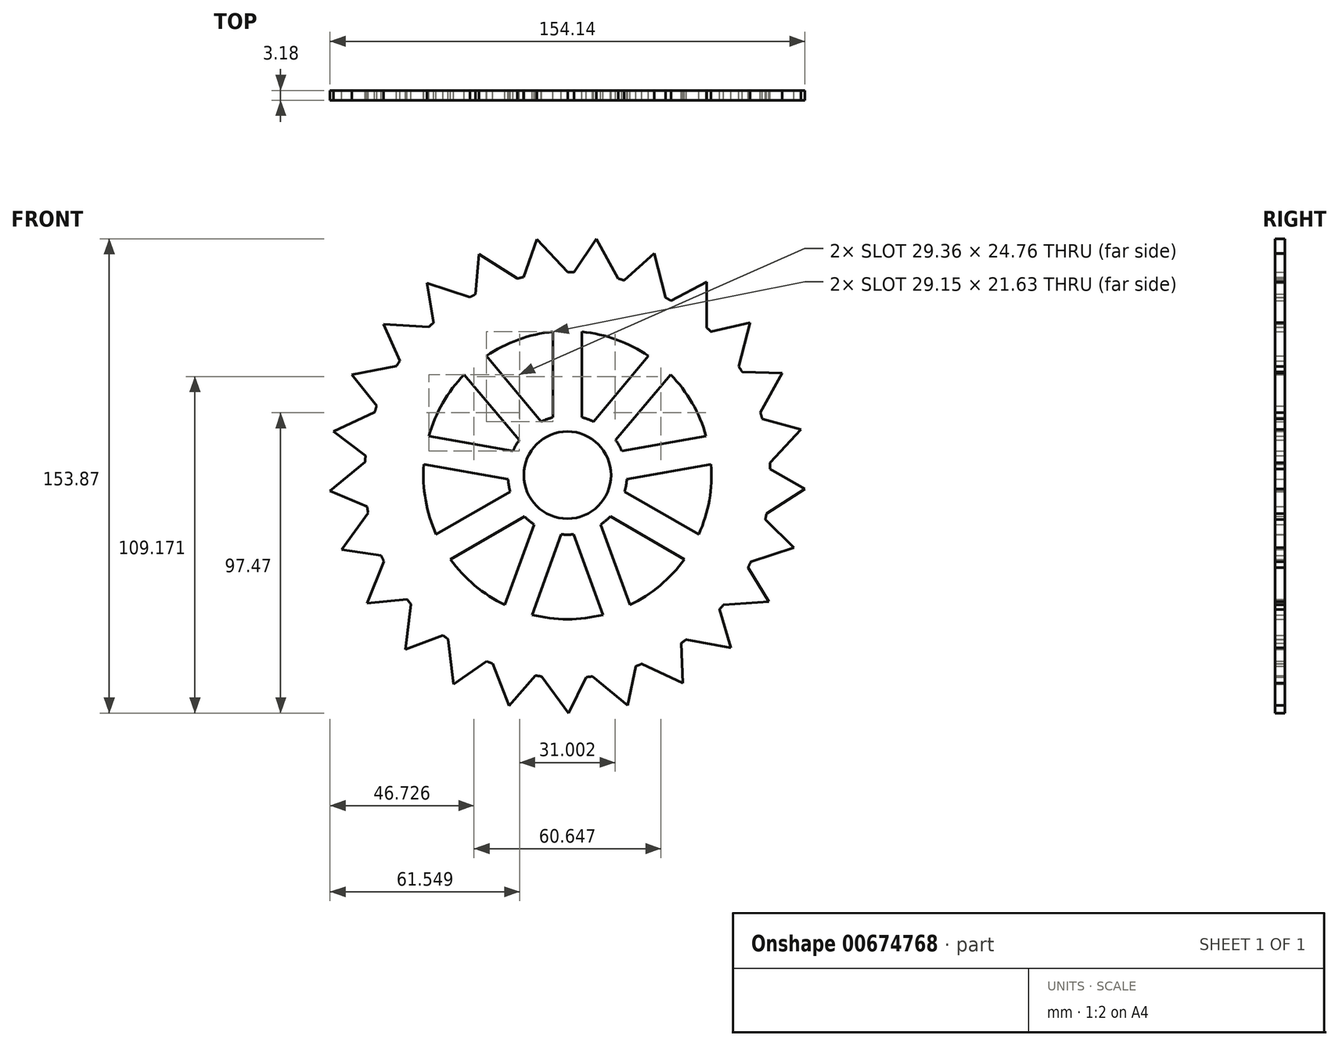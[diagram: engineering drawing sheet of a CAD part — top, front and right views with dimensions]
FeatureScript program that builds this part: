
annotation { "Feature Type Name" : "Feature", "Feature Type Description" : "" }
export const myFeature = defineFeature(function(context is Context, id is Id, definition is map)
    precondition{}
    {
        {
            var Q0;
            Q0=qCreatedBy(makeId("Front.planeOp"),FACE);
            var sketch = newSketch(context, id + "F0", { "sketchPlane" : qUnion([Q0])});
            skCircle(sketch, "E0", {"center": v(0, 0) * mm, "radius": 65.84 * mm});
            skLineSegment(sketch, "E1", {"start": v(33.58, 56.64) * mm, "end": v(45.14, 62.65) * mm});
            skLineSegment(sketch, "E2", {"start": v(45.14, 62.65) * mm, "end": v(45.14, 47.93) * mm});
            skLineSegment(sketch, "E3.1.0", {"start": v(28.14, 71.91) * mm, "end": v(31.8, 57.65) * mm});
            skLineSegment(sketch, "E3.1.1", {"start": v(18.44, 63.21) * mm, "end": v(28.14, 71.91) * mm});
            skLineSegment(sketch, "E3.2.0", {"start": v(9.38, 76.65) * mm, "end": v(16.47, 63.75) * mm});
            skLineSegment(sketch, "E3.2.1", {"start": v(2.14, 65.8) * mm, "end": v(9.38, 76.65) * mm});
            skLineSegment(sketch, "E3.3.0", {"start": v(-9.98, 76.57) * mm, "end": v(0.1, 65.84) * mm});
            skLineSegment(sketch, "E3.3.1", {"start": v(-14.3, 64.27) * mm, "end": v(-9.98, 76.57) * mm});
            skLineSegment(sketch, "E3.4.0", {"start": v(-28.7, 71.69) * mm, "end": v(-16.28, 63.8) * mm});
            skLineSegment(sketch, "E3.4.1", {"start": v(-29.83, 58.7) * mm, "end": v(-28.7, 71.69) * mm});
            skLineSegment(sketch, "E3.5.0", {"start": v(-45.63, 62.3) * mm, "end": v(-31.64, 57.75) * mm});
            skLineSegment(sketch, "E3.5.1", {"start": v(-43.49, 49.44) * mm, "end": v(-45.63, 62.3) * mm});
            skLineSegment(sketch, "E3.6.0", {"start": v(-59.7, 48.99) * mm, "end": v(-45, 48.06) * mm});
            skLineSegment(sketch, "E3.6.1", {"start": v(-54.42, 37.07) * mm, "end": v(-59.7, 48.99) * mm});
            skLineSegment(sketch, "E3.7.0", {"start": v(-70, 32.6) * mm, "end": v(-55.54, 35.36) * mm});
            skLineSegment(sketch, "E3.7.1", {"start": v(-61.93, 22.37) * mm, "end": v(-70, 32.6) * mm});
            skLineSegment(sketch, "E3.8.0", {"start": v(-75.91, 14.17) * mm, "end": v(-62.6, 20.44) * mm});
            skLineSegment(sketch, "E3.8.1", {"start": v(-65.55, 6.27) * mm, "end": v(-75.91, 14.17) * mm});
            skLineSegment(sketch, "E3.9.0", {"start": v(-77.05, -5.15) * mm, "end": v(-65.7, 4.23) * mm});
            skLineSegment(sketch, "E3.9.1", {"start": v(-65.05, -10.23) * mm, "end": v(-77.05, -5.15) * mm});
            skLineSegment(sketch, "E3.10.0", {"start": v(-73.35, -24.15) * mm, "end": v(-64.7, -12.24) * mm});
            skLineSegment(sketch, "E3.10.1", {"start": v(-60.46, -26.08) * mm, "end": v(-73.35, -24.15) * mm});
            skLineSegment(sketch, "E3.11.0", {"start": v(-65.04, -41.63) * mm, "end": v(-59.62, -27.95) * mm});
            skLineSegment(sketch, "E3.11.1", {"start": v(-52.07, -40.3) * mm, "end": v(-65.04, -41.63) * mm});
            skLineSegment(sketch, "E3.12.0", {"start": v(-52.64, -56.5) * mm, "end": v(-50.8, -41.9) * mm});
            skLineSegment(sketch, "E3.12.1", {"start": v(-40.41, -51.98) * mm, "end": v(-52.64, -56.5) * mm});
            skLineSegment(sketch, "E3.13.0", {"start": v(-36.94, -67.82) * mm, "end": v(-38.78, -53.21) * mm});
            skLineSegment(sketch, "E3.13.1", {"start": v(-26.22, -60.4) * mm, "end": v(-36.94, -67.82) * mm});
            skLineSegment(sketch, "E3.14.0", {"start": v(-18.91, -74.87) * mm, "end": v(-24.33, -61.19) * mm});
            skLineSegment(sketch, "E3.14.1", {"start": v(-10.37, -65.02) * mm, "end": v(-18.91, -74.87) * mm});
            skLineSegment(sketch, "E3.15.0", {"start": v(0.3, -77.22) * mm, "end": v(-8.35, -65.31) * mm});
            skLineSegment(sketch, "E3.15.1", {"start": v(6.12, -65.56) * mm, "end": v(0.3, -77.22) * mm});
            skLineSegment(sketch, "E3.16.0", {"start": v(19.5, -74.72) * mm, "end": v(8.16, -65.34) * mm});
            skLineSegment(sketch, "E3.16.1", {"start": v(22.24, -61.98) * mm, "end": v(19.5, -74.72) * mm});
            skLineSegment(sketch, "E3.17.0", {"start": v(37.47, -67.52) * mm, "end": v(24.15, -61.26) * mm});
            skLineSegment(sketch, "E3.17.1", {"start": v(36.95, -54.5) * mm, "end": v(37.47, -67.52) * mm});
            skLineSegment(sketch, "E3.18.0", {"start": v(53.08, -56.08) * mm, "end": v(38.62, -53.33) * mm});
            skLineSegment(sketch, "E3.18.1", {"start": v(49.34, -43.6) * mm, "end": v(53.08, -56.08) * mm});
            skLineSegment(sketch, "E3.19.0", {"start": v(65.36, -41.12) * mm, "end": v(50.67, -42.05) * mm});
            skLineSegment(sketch, "E3.19.1", {"start": v(58.64, -29.96) * mm, "end": v(65.36, -41.12) * mm});
            skLineSegment(sketch, "E3.20.0", {"start": v(73.54, -23.57) * mm, "end": v(59.54, -28.12) * mm});
            skLineSegment(sketch, "E3.20.1", {"start": v(64.24, -14.43) * mm, "end": v(73.54, -23.57) * mm});
            skLineSegment(sketch, "E3.21.0", {"start": v(77.09, -4.55) * mm, "end": v(64.66, -12.43) * mm});
            skLineSegment(sketch, "E3.21.1", {"start": v(65.81, 2) * mm, "end": v(77.09, -4.55) * mm});
            skLineSegment(sketch, "E3.22.0", {"start": v(75.8, 14.77) * mm, "end": v(65.72, 4.04) * mm});
            skLineSegment(sketch, "E3.22.1", {"start": v(63.25, 18.3) * mm, "end": v(75.8, 14.77) * mm});
            skLineSegment(sketch, "E3.23.0", {"start": v(69.74, 33.15) * mm, "end": v(62.65, 20.26) * mm});
            skLineSegment(sketch, "E3.23.1", {"start": v(56.71, 33.46) * mm, "end": v(69.74, 33.15) * mm});
            skLineSegment(sketch, "E3.24.0", {"start": v(59.3, 49.46) * mm, "end": v(55.65, 35.2) * mm});
            skLineSegment(sketch, "E3.24.1", {"start": v(46.61, 46.5) * mm, "end": v(59.3, 49.46) * mm});
            skCircle(sketch, "E4", {"center": v(0, 0) * mm, "radius": 14.14 * mm});
            skCircle(sketch, "E5", {"center": v(0, 0) * mm, "radius": 46.76 * mm});
            skLineSegment(sketch, "E6", {"start": v(-4.68, 13.35) * mm, "end": v(-4.68, 46.53) * mm});
            skLineSegment(sketch, "E7", {"start": v(4.68, 13.35) * mm, "end": v(4.68, 46.53) * mm});
            skLineSegment(sketch, "E8.1.0", {"start": v(-4.99, 13.23) * mm, "end": v(-26.32, 38.65) * mm});
            skLineSegment(sketch, "E8.1.1", {"start": v(-12.17, 7.21) * mm, "end": v(-33.5, 32.63) * mm});
            skLineSegment(sketch, "E8.2.0", {"start": v(-12.33, 6.93) * mm, "end": v(-45, 12.7) * mm});
            skLineSegment(sketch, "E8.2.1", {"start": v(-13.96, -2.3) * mm, "end": v(-46.63, 3.47) * mm});
            skLineSegment(sketch, "E8.3.0", {"start": v(-13.9, -2.62) * mm, "end": v(-42.63, -19.2) * mm});
            skLineSegment(sketch, "E8.3.1", {"start": v(-9.22, -10.73) * mm, "end": v(-37.95, -27.32) * mm});
            skLineSegment(sketch, "E8.4.0", {"start": v(-8.97, -10.94) * mm, "end": v(-20.31, -42.12) * mm});
            skLineSegment(sketch, "E8.4.1", {"start": v(-0.16, -14.14) * mm, "end": v(-11.51, -45.32) * mm});
            skLineSegment(sketch, "E8.5.0", {"start": v(0.16, -14.14) * mm, "end": v(11.51, -45.32) * mm});
            skLineSegment(sketch, "E8.5.1", {"start": v(8.97, -10.94) * mm, "end": v(20.31, -42.12) * mm});
            skLineSegment(sketch, "E8.6.0", {"start": v(9.22, -10.73) * mm, "end": v(37.95, -27.32) * mm});
            skLineSegment(sketch, "E8.6.1", {"start": v(13.9, -2.62) * mm, "end": v(42.63, -19.2) * mm});
            skLineSegment(sketch, "E8.7.0", {"start": v(13.96, -2.3) * mm, "end": v(46.63, 3.47) * mm});
            skLineSegment(sketch, "E8.7.1", {"start": v(12.33, 6.93) * mm, "end": v(45, 12.7) * mm});
            skLineSegment(sketch, "E8.8.0", {"start": v(12.17, 7.21) * mm, "end": v(33.5, 32.63) * mm});
            skLineSegment(sketch, "E8.8.1", {"start": v(4.99, 13.23) * mm, "end": v(26.32, 38.65) * mm});
            skCircle(sketch, "E9", {"center": v(0, 0) * mm, "radius": 19.33 * mm});
            skSolve(sketch);
        }
        {
            var Q0;
            {var subQ0=sQuery(id+"F0.wireOp",EDGE,"E0");var subQ52=makeQuery(id+"F0.imprint","INTERSECT",VERTEX,{"derivedFrom":[subQ0,sQuery(id+"F0.wireOp",EDGE,"E3.21.1")]});Q0=makeQuery(id+"F0.imprint","IMPRINT",FACE,{"disambiguationData":[TD([[makeQuery(id+"F0.imprint","IMPRINT",EDGE,{"disambiguationData":[TD([[subQ52,-1.0]])],"derivedFrom":subQ0}),1.0]])]});}
            var Q1;
            {var subQ0=sQuery(id+"F0.wireOp",EDGE,"E8.8.0");Q1=makeQuery(id+"F0.imprint","IMPRINT",FACE,{"disambiguationData":[TD([[makeQuery(id+"F0.imprint","IMPRINT",EDGE,{"derivedFrom":subQ0}),1.0]])]});}
            var Q2;
            {var subQ0=sQuery(id+"F0.wireOp",EDGE,"E6");Q2=makeQuery(id+"F0.imprint","IMPRINT",FACE,{"disambiguationData":[TD([[makeQuery(id+"F0.imprint","IMPRINT",EDGE,{"derivedFrom":subQ0}),-1.0]])]});}
            var Q3;
            {var subQ0=sQuery(id+"F0.wireOp",EDGE,"E8.7.0");Q3=makeQuery(id+"F0.imprint","IMPRINT",FACE,{"disambiguationData":[TD([[makeQuery(id+"F0.imprint","IMPRINT",EDGE,{"derivedFrom":subQ0}),1.0]])]});}
            var Q4;
            {var subQ0=sQuery(id+"F0.wireOp",EDGE,"E8.6.0");Q4=makeQuery(id+"F0.imprint","IMPRINT",FACE,{"disambiguationData":[TD([[makeQuery(id+"F0.imprint","IMPRINT",EDGE,{"derivedFrom":subQ0}),1.0]])]});}
            var Q5;
            {var subQ0=sQuery(id+"F0.wireOp",EDGE,"E8.5.0");Q5=makeQuery(id+"F0.imprint","IMPRINT",FACE,{"disambiguationData":[TD([[makeQuery(id+"F0.imprint","IMPRINT",EDGE,{"derivedFrom":subQ0}),1.0]])]});}
            var Q6;
            {var subQ0=sQuery(id+"F0.wireOp",EDGE,"E8.4.0");Q6=makeQuery(id+"F0.imprint","IMPRINT",FACE,{"disambiguationData":[TD([[makeQuery(id+"F0.imprint","IMPRINT",EDGE,{"derivedFrom":subQ0}),1.0]])]});}
            var Q7;
            {var subQ0=sQuery(id+"F0.wireOp",EDGE,"E8.3.0");Q7=makeQuery(id+"F0.imprint","IMPRINT",FACE,{"disambiguationData":[TD([[makeQuery(id+"F0.imprint","IMPRINT",EDGE,{"derivedFrom":subQ0}),1.0]])]});}
            var Q8;
            {var subQ0=sQuery(id+"F0.wireOp",EDGE,"E8.2.0");Q8=makeQuery(id+"F0.imprint","IMPRINT",FACE,{"disambiguationData":[TD([[makeQuery(id+"F0.imprint","IMPRINT",EDGE,{"derivedFrom":subQ0}),1.0]])]});}
            var Q9;
            {var subQ0=sQuery(id+"F0.wireOp",EDGE,"E8.1.0");Q9=makeQuery(id+"F0.imprint","IMPRINT",FACE,{"disambiguationData":[TD([[makeQuery(id+"F0.imprint","IMPRINT",EDGE,{"derivedFrom":subQ0}),1.0]])]});}
            var Q10;
            {var subQ0=sQuery(id+"F0.wireOp",EDGE,"E3.21.0");Q10=makeQuery(id+"F0.imprint","IMPRINT",FACE,{"disambiguationData":[TD([[makeQuery(id+"F0.imprint","IMPRINT",EDGE,{"derivedFrom":subQ0}),-1.0]])]});}
            var Q11;
            {var subQ0=sQuery(id+"F0.wireOp",EDGE,"E3.22.0");Q11=makeQuery(id+"F0.imprint","IMPRINT",FACE,{"disambiguationData":[TD([[makeQuery(id+"F0.imprint","IMPRINT",EDGE,{"derivedFrom":subQ0}),-1.0]])]});}
            var Q12;
            {var subQ0=sQuery(id+"F0.wireOp",EDGE,"E3.23.0");Q12=makeQuery(id+"F0.imprint","IMPRINT",FACE,{"disambiguationData":[TD([[makeQuery(id+"F0.imprint","IMPRINT",EDGE,{"derivedFrom":subQ0}),-1.0]])]});}
            var Q13;
            {var subQ0=sQuery(id+"F0.wireOp",EDGE,"E3.24.0");Q13=makeQuery(id+"F0.imprint","IMPRINT",FACE,{"disambiguationData":[TD([[makeQuery(id+"F0.imprint","IMPRINT",EDGE,{"derivedFrom":subQ0}),-1.0]])]});}
            var Q14;
            {var subQ0=sQuery(id+"F0.wireOp",EDGE,"E1");Q14=makeQuery(id+"F0.imprint","IMPRINT",FACE,{"disambiguationData":[TD([[makeQuery(id+"F0.imprint","IMPRINT",EDGE,{"derivedFrom":subQ0}),-1.0]])]});}
            var Q15;
            {var subQ0=sQuery(id+"F0.wireOp",EDGE,"E3.1.0");Q15=makeQuery(id+"F0.imprint","IMPRINT",FACE,{"disambiguationData":[TD([[makeQuery(id+"F0.imprint","IMPRINT",EDGE,{"derivedFrom":subQ0}),-1.0]])]});}
            var Q16;
            {var subQ0=sQuery(id+"F0.wireOp",EDGE,"E3.2.0");Q16=makeQuery(id+"F0.imprint","IMPRINT",FACE,{"disambiguationData":[TD([[makeQuery(id+"F0.imprint","IMPRINT",EDGE,{"derivedFrom":subQ0}),-1.0]])]});}
            var Q17;
            {var subQ0=sQuery(id+"F0.wireOp",EDGE,"E3.3.0");Q17=makeQuery(id+"F0.imprint","IMPRINT",FACE,{"disambiguationData":[TD([[makeQuery(id+"F0.imprint","IMPRINT",EDGE,{"derivedFrom":subQ0}),-1.0]])]});}
            var Q18;
            {var subQ0=sQuery(id+"F0.wireOp",EDGE,"E3.4.0");Q18=makeQuery(id+"F0.imprint","IMPRINT",FACE,{"disambiguationData":[TD([[makeQuery(id+"F0.imprint","IMPRINT",EDGE,{"derivedFrom":subQ0}),-1.0]])]});}
            var Q19;
            {var subQ0=sQuery(id+"F0.wireOp",EDGE,"E3.5.0");Q19=makeQuery(id+"F0.imprint","IMPRINT",FACE,{"disambiguationData":[TD([[makeQuery(id+"F0.imprint","IMPRINT",EDGE,{"derivedFrom":subQ0}),-1.0]])]});}
            var Q20;
            {var subQ0=sQuery(id+"F0.wireOp",EDGE,"E3.6.0");Q20=makeQuery(id+"F0.imprint","IMPRINT",FACE,{"disambiguationData":[TD([[makeQuery(id+"F0.imprint","IMPRINT",EDGE,{"derivedFrom":subQ0}),-1.0]])]});}
            var Q21;
            {var subQ0=sQuery(id+"F0.wireOp",EDGE,"E3.7.0");Q21=makeQuery(id+"F0.imprint","IMPRINT",FACE,{"disambiguationData":[TD([[makeQuery(id+"F0.imprint","IMPRINT",EDGE,{"derivedFrom":subQ0}),-1.0]])]});}
            var Q22;
            {var subQ0=sQuery(id+"F0.wireOp",EDGE,"E3.8.0");Q22=makeQuery(id+"F0.imprint","IMPRINT",FACE,{"disambiguationData":[TD([[makeQuery(id+"F0.imprint","IMPRINT",EDGE,{"derivedFrom":subQ0}),-1.0]])]});}
            var Q23;
            {var subQ0=sQuery(id+"F0.wireOp",EDGE,"E3.9.0");Q23=makeQuery(id+"F0.imprint","IMPRINT",FACE,{"disambiguationData":[TD([[makeQuery(id+"F0.imprint","IMPRINT",EDGE,{"derivedFrom":subQ0}),-1.0]])]});}
            var Q24;
            {var subQ0=sQuery(id+"F0.wireOp",EDGE,"E3.11.0");Q24=makeQuery(id+"F0.imprint","IMPRINT",FACE,{"disambiguationData":[TD([[makeQuery(id+"F0.imprint","IMPRINT",EDGE,{"derivedFrom":subQ0}),-1.0]])]});}
            var Q25;
            {var subQ0=sQuery(id+"F0.wireOp",EDGE,"E3.12.0");Q25=makeQuery(id+"F0.imprint","IMPRINT",FACE,{"disambiguationData":[TD([[makeQuery(id+"F0.imprint","IMPRINT",EDGE,{"derivedFrom":subQ0}),-1.0]])]});}
            var Q26;
            {var subQ0=sQuery(id+"F0.wireOp",EDGE,"E3.13.0");Q26=makeQuery(id+"F0.imprint","IMPRINT",FACE,{"disambiguationData":[TD([[makeQuery(id+"F0.imprint","IMPRINT",EDGE,{"derivedFrom":subQ0}),-1.0]])]});}
            var Q27;
            {var subQ0=sQuery(id+"F0.wireOp",EDGE,"E3.14.0");Q27=makeQuery(id+"F0.imprint","IMPRINT",FACE,{"disambiguationData":[TD([[makeQuery(id+"F0.imprint","IMPRINT",EDGE,{"derivedFrom":subQ0}),-1.0]])]});}
            var Q28;
            {var subQ0=sQuery(id+"F0.wireOp",EDGE,"E3.15.0");Q28=makeQuery(id+"F0.imprint","IMPRINT",FACE,{"disambiguationData":[TD([[makeQuery(id+"F0.imprint","IMPRINT",EDGE,{"derivedFrom":subQ0}),-1.0]])]});}
            var Q29;
            {var subQ0=sQuery(id+"F0.wireOp",EDGE,"E3.16.0");Q29=makeQuery(id+"F0.imprint","IMPRINT",FACE,{"disambiguationData":[TD([[makeQuery(id+"F0.imprint","IMPRINT",EDGE,{"derivedFrom":subQ0}),-1.0]])]});}
            var Q30;
            {var subQ0=sQuery(id+"F0.wireOp",EDGE,"E3.17.0");Q30=makeQuery(id+"F0.imprint","IMPRINT",FACE,{"disambiguationData":[TD([[makeQuery(id+"F0.imprint","IMPRINT",EDGE,{"derivedFrom":subQ0}),-1.0]])]});}
            var Q31;
            {var subQ0=sQuery(id+"F0.wireOp",EDGE,"E3.18.0");Q31=makeQuery(id+"F0.imprint","IMPRINT",FACE,{"disambiguationData":[TD([[makeQuery(id+"F0.imprint","IMPRINT",EDGE,{"derivedFrom":subQ0}),-1.0]])]});}
            var Q32;
            {var subQ0=sQuery(id+"F0.wireOp",EDGE,"E3.19.0");Q32=makeQuery(id+"F0.imprint","IMPRINT",FACE,{"disambiguationData":[TD([[makeQuery(id+"F0.imprint","IMPRINT",EDGE,{"derivedFrom":subQ0}),-1.0]])]});}
            var Q33;
            {var subQ0=sQuery(id+"F0.wireOp",EDGE,"E3.20.0");Q33=makeQuery(id+"F0.imprint","IMPRINT",FACE,{"disambiguationData":[TD([[makeQuery(id+"F0.imprint","IMPRINT",EDGE,{"derivedFrom":subQ0}),-1.0]])]});}
            var Q34;
            {var subQ0=sQuery(id+"F0.wireOp",EDGE,"E3.10.0");Q34=makeQuery(id+"F0.imprint","IMPRINT",FACE,{"disambiguationData":[TD([[makeQuery(id+"F0.imprint","IMPRINT",EDGE,{"derivedFrom":subQ0}),-1.0]])]});}
            var Q35;
            {var subQ0=sQuery(id+"F0.wireOp",EDGE,"E8.2.1");var subQ1=sQuery(id+"F0.wireOp",EDGE,"E4");var subQ2=makeQuery(id+"F0.imprint","INTERSECT",VERTEX,{"derivedFrom":[subQ1,subQ0]});Q35=makeQuery(id+"F0.imprint","IMPRINT",FACE,{"disambiguationData":[TD([[makeQuery(id+"F0.imprint","IMPRINT",EDGE,{"disambiguationData":[TD([[subQ2,-1.0]])],"derivedFrom":subQ1}),-1.0]])]});}
            var Q36;
            {var subQ0=sQuery(id+"F0.wireOp",EDGE,"E8.1.1");var subQ1=sQuery(id+"F0.wireOp",EDGE,"E4");var subQ2=makeQuery(id+"F0.imprint","INTERSECT",VERTEX,{"derivedFrom":[subQ1,subQ0]});Q36=makeQuery(id+"F0.imprint","IMPRINT",FACE,{"disambiguationData":[TD([[makeQuery(id+"F0.imprint","IMPRINT",EDGE,{"disambiguationData":[TD([[subQ2,-1.0]])],"derivedFrom":subQ1}),-1.0]])]});}
            var Q37;
            {var subQ0=sQuery(id+"F0.wireOp",EDGE,"E6");var subQ1=sQuery(id+"F0.wireOp",EDGE,"E4");var subQ2=makeQuery(id+"F0.imprint","INTERSECT",VERTEX,{"derivedFrom":[subQ1,subQ0]});Q37=makeQuery(id+"F0.imprint","IMPRINT",FACE,{"disambiguationData":[TD([[makeQuery(id+"F0.imprint","IMPRINT",EDGE,{"disambiguationData":[TD([[subQ2,-1.0]])],"derivedFrom":subQ1}),-1.0]])]});}
            var Q38;
            {var subQ0=sQuery(id+"F0.wireOp",EDGE,"E7");var subQ1=sQuery(id+"F0.wireOp",EDGE,"E4");var subQ2=makeQuery(id+"F0.imprint","INTERSECT",VERTEX,{"derivedFrom":[subQ1,subQ0]});Q38=makeQuery(id+"F0.imprint","IMPRINT",FACE,{"disambiguationData":[TD([[makeQuery(id+"F0.imprint","IMPRINT",EDGE,{"disambiguationData":[TD([[subQ2,1.0]])],"derivedFrom":subQ1}),-1.0]])]});}
            var Q39;
            {var subQ0=sQuery(id+"F0.wireOp",EDGE,"E8.7.1");var subQ1=sQuery(id+"F0.wireOp",EDGE,"E4");var subQ2=makeQuery(id+"F0.imprint","INTERSECT",VERTEX,{"derivedFrom":[subQ1,subQ0]});Q39=makeQuery(id+"F0.imprint","IMPRINT",FACE,{"disambiguationData":[TD([[makeQuery(id+"F0.imprint","IMPRINT",EDGE,{"disambiguationData":[TD([[subQ2,-1.0]])],"derivedFrom":subQ1}),-1.0]])]});}
            var Q40;
            {var subQ0=sQuery(id+"F0.wireOp",EDGE,"E8.6.1");var subQ1=sQuery(id+"F0.wireOp",EDGE,"E4");var subQ2=makeQuery(id+"F0.imprint","INTERSECT",VERTEX,{"derivedFrom":[subQ1,subQ0]});Q40=makeQuery(id+"F0.imprint","IMPRINT",FACE,{"disambiguationData":[TD([[makeQuery(id+"F0.imprint","IMPRINT",EDGE,{"disambiguationData":[TD([[subQ2,-1.0]])],"derivedFrom":subQ1}),-1.0]])]});}
            var Q41;
            {var subQ0=sQuery(id+"F0.wireOp",EDGE,"E8.5.1");var subQ1=sQuery(id+"F0.wireOp",EDGE,"E4");var subQ2=makeQuery(id+"F0.imprint","INTERSECT",VERTEX,{"derivedFrom":[subQ1,subQ0]});Q41=makeQuery(id+"F0.imprint","IMPRINT",FACE,{"disambiguationData":[TD([[makeQuery(id+"F0.imprint","IMPRINT",EDGE,{"disambiguationData":[TD([[subQ2,-1.0]])],"derivedFrom":subQ1}),-1.0]])]});}
            var Q42;
            {var subQ0=sQuery(id+"F0.wireOp",EDGE,"E8.4.1");var subQ1=sQuery(id+"F0.wireOp",EDGE,"E4");var subQ2=makeQuery(id+"F0.imprint","INTERSECT",VERTEX,{"derivedFrom":[subQ1,subQ0]});Q42=makeQuery(id+"F0.imprint","IMPRINT",FACE,{"disambiguationData":[TD([[makeQuery(id+"F0.imprint","IMPRINT",EDGE,{"disambiguationData":[TD([[subQ2,-1.0]])],"derivedFrom":subQ1}),-1.0]])]});}
            var Q43;
            {var subQ0=sQuery(id+"F0.wireOp",EDGE,"E8.3.1");var subQ1=sQuery(id+"F0.wireOp",EDGE,"E4");var subQ2=makeQuery(id+"F0.imprint","INTERSECT",VERTEX,{"derivedFrom":[subQ1,subQ0]});Q43=makeQuery(id+"F0.imprint","IMPRINT",FACE,{"disambiguationData":[TD([[makeQuery(id+"F0.imprint","IMPRINT",EDGE,{"disambiguationData":[TD([[subQ2,-1.0]])],"derivedFrom":subQ1}),-1.0]])]});}
            extrude(context, id + "F1", {"entities" : qUnion([Q0, Q1, Q2, Q3, Q4, Q5, Q6, Q7, Q8, Q9, Q10, Q11, Q12, Q13, Q14, Q15, Q16, Q17, Q18, Q19, Q20, Q21, Q22, Q23, Q24, Q25, Q26, Q27, Q28, Q29, Q30, Q31, Q32, Q33, Q34, Q35, Q36, Q37, Q38, Q39, Q40, Q41, Q42, Q43]), "depth" : 3.17 * mm, "offsetDistance" : 25.4 * mm});
        }
    });
